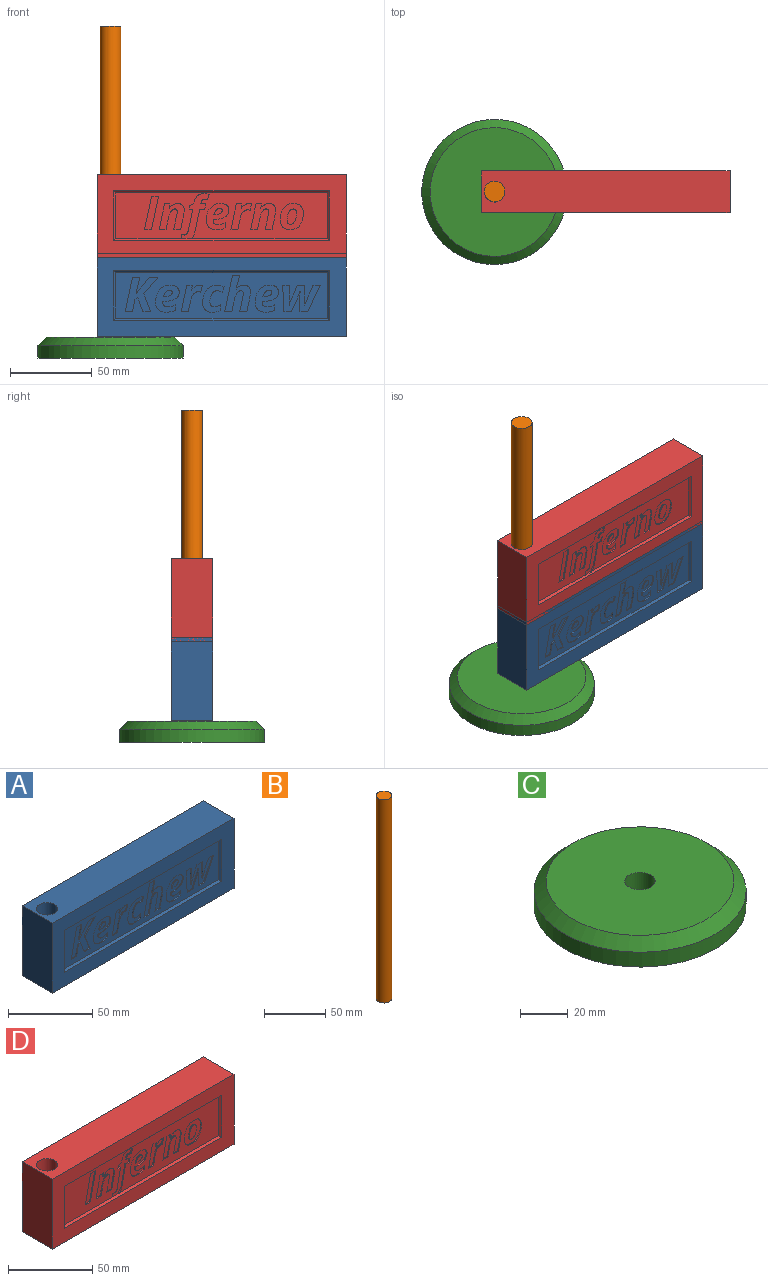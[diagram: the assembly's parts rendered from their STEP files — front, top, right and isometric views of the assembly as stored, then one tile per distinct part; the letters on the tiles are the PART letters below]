
ASSEMBLY  parts=4 mates=5
PART A: 157 faces, bbox 152.4x25.4x50.8 mm
  f0: plane 129.54x27.94mm, normal (0,-1,0), area 2509.1mm2, adj f8,f9,f10,f11,f12,f13,f14,f15
  f1: plane 152.4x50.8mm, normal (0,-1,0), area 3716.1mm2, adj f2,f3,f4,f5,f8,f9,f10,f11
  f2: plane 50.8x25.4mm, normal (1,0,0), area 1290.3mm2, adj f1,f3,f5,f6
  f3: plane 152.4x25.4mm, normal (0,0,1), area 3744.3mm2, adj f1,f2,f4,f6,f7
  f4: plane 50.8x25.4mm, normal (-1,0,0), area 1290.3mm2, adj f1,f3,f5,f6
  f5: plane 152.4x25.4mm, normal (0,0,-1), area 3744.3mm2, adj f1,f2,f4,f6,f7
  f6: plane 152.4x50.8mm, normal (0,1,0), area 7741.9mm2, adj f2,f3,f4,f5
  f7: cylinder r=6.35mm len=50.8mm, axis (0,0,1), area 2026.8mm2, adj f3,f5
  f8: plane 30.48x1.27mm, normal (0.71,-0.71,0), area 52.5mm2, adj f0,f1,f9,f10
  f9: plane 132.08x1.27mm, normal (0,-0.71,-0.71), area 234.9mm2, adj f0,f1,f8,f11
  f10: plane 132.08x1.27mm, normal (0,-0.71,0.71), area 234.9mm2, adj f0,f1,f8,f11
  f11: plane 30.48x1.27mm, normal (-0.71,-0.71,0), area 52.5mm2, adj f0,f1,f9,f10
  f12: plane 4.87x0.76mm, normal (0,0,1), area 3.7mm2, adj f0,f13,f24,f25
  f13: plane 10.97x4.19mm, normal (-0.93,0,-0.36), area 8.9mm2, adj f0,f12,f14,f25
  f14: plane 10.08x8.55mm, normal (-0.76,0,0.65), area 10.1mm2, adj f0,f13,f15,f25
  f15: plane 5.2x0.76mm, normal (0,0,-1), area 4mm2, adj f0,f14,f16,f25
  f16: plane 7.15x5.89mm, normal (0.77,0,-0.64), area 7.1mm2, adj f0,f15,f17,f25
  f17: plane 2.95x2.27mm, normal (0.79,0,-0.61), area 2.8mm2, adj f0,f16,f18,f25
  f18: plane 10.11x2.19mm, normal (-0.98,0,0.21), area 7.9mm2, adj f0,f17,f19,f25
  f19: plane 4.41x0.76mm, normal (0,0,-1), area 3.4mm2, adj f0,f18,f20,f25
  f20: plane 21.05x4.45mm, normal (0.98,0,-0.21), area 16.4mm2, adj f0,f19,f21,f25
  f21: plane 4.39x0.76mm, normal (0,0,1), area 3.3mm2, adj f0,f20,f22,f25
  f22: plane 7.51x1.57mm, normal (-0.98,0,0.2), area 5.8mm2, adj f0,f21,f23,f25
  f23: plane 1.8x1.01mm, normal (-0.49,0,0.87), area 1.6mm2, adj f0,f22,f24,f25
  f24: plane 8.52x3.04mm, normal (0.94,0,0.34), area 6.9mm2, adj f0,f12,f23,f25
  f25: plane 21.05x20.02mm, normal (0,-1,0), area 197.8mm2, adj f12,f13,f14,f15,f16,f17,f18,f19
  f26: extruded ~4.7x1.63mm, area 3.9mm2, adj f0,f27,f49,f50
  f27: extruded ~5.61x1.24mm, area 4.4mm2, adj f0,f26,f28,f50
  f28: plane 3.27x0.76mm, normal (-1,0,0), area 2.5mm2, adj f0,f27,f29,f50
  f29: extruded ~2.47x0.97mm, area 2mm2, adj f0,f28,f30,f50
  f30: extruded ~2.28x0.76mm, area 1.8mm2, adj f0,f29,f31,f50
  f31: extruded ~2.12x0.76mm, area 1.8mm2, adj f0,f30,f32,f50
  f32: extruded ~2.06x0.76mm, area 1.7mm2, adj f0,f31,f33,f50
  f33: plane 0.76x0.29mm, normal (-1,0,0), area 0.2mm2, adj f0,f32,f34,f50
  f34: plane 0.76x0.3mm, normal (-1,0,0.09), area 0.2mm2, adj f0,f33,f35,f50
  f35: plane 0.76x0.74mm, normal (0,0,1), area 0.6mm2, adj f0,f34,f36,f50
  f36: extruded ~6.87x1.46mm, area 5.4mm2, adj f0,f35,f37,f50
  f37: extruded ~4.15x2.4mm, area 3.8mm2, adj f0,f36,f38,f50
  f38: extruded ~3.22x1.42mm, area 2.8mm2, adj f0,f37,f39,f50
  f39: extruded ~3.98x1.17mm, area 3.2mm2, adj f0,f38,f40,f50
  f40: extruded ~4.59x1.29mm, area 3.7mm2, adj f0,f39,f41,f50
  f41: extruded ~3.74x3.22mm, area 3.8mm2, adj f0,f40,f42,f50
  f42: extruded ~5.43x1.19mm, area 4.3mm2, adj f0,f41,f49,f50
  f43: extruded ~2.39x1.15mm, area 2.1mm2, adj f44,f48,f50,f51
  f44: extruded ~1.51x1.37mm, area 1.8mm2, adj f43,f45,f50,f51
  f45: extruded ~1.89x1.24mm, area 1.8mm2, adj f44,f46,f50,f51
  f46: extruded ~3.48x0.76mm, area 2.7mm2, adj f45,f47,f50,f51
  f47: plane 0.76x0.65mm, normal (0,0,-1), area 0.5mm2, adj f46,f48,f50,f51
  f48: extruded ~2.81x1.47mm, area 2.4mm2, adj f43,f47,f50,f51
  f49: extruded ~4.59x1.67mm, area 3.8mm2, adj f0,f26,f42,f50
  f50: plane 16.68x14.39mm, normal (0,-1,0), area 145.3mm2, adj f26,f27,f28,f29,f30,f31,f32,f33
  f51: plane 5.37x3.96mm, normal (0,-1,0), area 14.5mm2, adj f43,f44,f45,f46,f47,f48
  f52: extruded ~4.7x1.63mm, area 3.9mm2, adj f0,f53,f75,f76
  f53: extruded ~5.61x1.24mm, area 4.4mm2, adj f0,f52,f54,f76
  f54: plane 3.27x0.76mm, normal (-1,0,0), area 2.5mm2, adj f0,f53,f55,f76
  f55: extruded ~2.47x0.97mm, area 2mm2, adj f0,f54,f56,f76
  f56: extruded ~2.28x0.76mm, area 1.8mm2, adj f0,f55,f57,f76
  f57: extruded ~2.12x0.76mm, area 1.8mm2, adj f0,f56,f58,f76
  f58: extruded ~2.06x0.76mm, area 1.7mm2, adj f0,f57,f59,f76
  f59: plane 0.76x0.29mm, normal (-1,0,0), area 0.2mm2, adj f0,f58,f60,f76
  f60: plane 0.76x0.3mm, normal (-1,0,0.09), area 0.2mm2, adj f0,f59,f61,f76
  f61: plane 0.76x0.74mm, normal (0,0,1), area 0.6mm2, adj f0,f60,f62,f76
  f62: extruded ~6.87x1.46mm, area 5.4mm2, adj f0,f61,f63,f76
  f63: extruded ~4.15x2.4mm, area 3.8mm2, adj f0,f62,f64,f76
  f64: extruded ~3.22x1.42mm, area 2.8mm2, adj f0,f63,f65,f76
  f65: extruded ~3.98x1.17mm, area 3.2mm2, adj f0,f64,f66,f76
  f66: extruded ~4.59x1.29mm, area 3.7mm2, adj f0,f65,f67,f76
  f67: extruded ~3.74x3.22mm, area 3.8mm2, adj f0,f66,f68,f76
  f68: extruded ~5.43x1.19mm, area 4.3mm2, adj f0,f67,f75,f76
  f69: extruded ~2.39x1.15mm, area 2.1mm2, adj f70,f74,f76,f77
  f70: extruded ~1.51x1.37mm, area 1.8mm2, adj f69,f71,f76,f77
  f71: extruded ~1.89x1.24mm, area 1.8mm2, adj f70,f72,f76,f77
  f72: extruded ~3.48x0.76mm, area 2.7mm2, adj f71,f73,f76,f77
  f73: plane 0.76x0.65mm, normal (0,0,-1), area 0.5mm2, adj f72,f74,f76,f77
  f74: extruded ~2.81x1.47mm, area 2.4mm2, adj f69,f73,f76,f77
  f75: extruded ~4.59x1.67mm, area 3.8mm2, adj f0,f52,f68,f76
  f76: plane 16.68x14.39mm, normal (0,-1,0), area 145.3mm2, adj f52,f53,f54,f55,f56,f57,f58,f59
  f77: plane 5.37x3.96mm, normal (0,-1,0), area 14.5mm2, adj f69,f70,f71,f72,f73,f74
  f78: extruded ~4.59x1.77mm, area 3.8mm2, adj f0,f79,f103,f104
  f79: plane 0.76x0.09mm, normal (0,0,1), area 0.1mm2, adj f0,f78,f80,f104
  f80: extruded ~4.9x0.76mm, area 3.7mm2, adj f0,f79,f81,f104
  f81: plane 7.49x0.76mm, normal (1,0,0.01), area 5.7mm2, adj f0,f80,f82,f104
  f82: plane 4.75x0.76mm, normal (0,0,1), area 3.6mm2, adj f0,f81,f83,f104
  f83: plane 16.09x7.63mm, normal (-0.9,0,0.43), area 13.6mm2, adj f0,f82,f84,f104
  f84: plane 4.42x0.76mm, normal (0,0,-1), area 3.4mm2, adj f0,f83,f85,f104
  f85: plane 7.13x3.15mm, normal (0.91,0,-0.4), area 5.9mm2, adj f0,f84,f86,f104
  f86: extruded ~3.71x1.37mm, area 3mm2, adj f0,f85,f87,f104
  f87: plane 1.15x0.76mm, normal (0.94,0,-0.33), area 0.9mm2, adj f0,f86,f88,f104
  f88: plane 0.76x0.09mm, normal (0,0,-1), area 0.1mm2, adj f0,f87,f89,f104
  f89: extruded ~4.27x0.76mm, area 3.3mm2, adj f0,f88,f90,f104
  f90: plane 7.72x0.76mm, normal (-1,0,0), area 5.9mm2, adj f0,f89,f91,f104
  f91: plane 4.72x0.76mm, normal (0,0,-1), area 3.6mm2, adj f0,f90,f92,f104
  f92: plane 7.72x3.33mm, normal (0.92,0,-0.4), area 6.4mm2, adj f0,f91,f93,f104
  f93: extruded ~1.71x0.76mm, area 1.4mm2, adj f0,f92,f94,f104
  f94: extruded ~1.96x0.76mm, area 1.6mm2, adj f0,f93,f95,f104
  f95: extruded ~0.76x0.6mm, area 0.5mm2, adj f0,f94,f96,f104
  f96: plane 0.76x0.06mm, normal (0,0,-1), area 0mm2, adj f0,f95,f97,f104
  f97: plane 2.46x0.76mm, normal (-1,0,0.04), area 1.9mm2, adj f0,f96,f98,f104
  f98: plane 2.4x0.76mm, normal (-1,0,0.02), area 1.8mm2, adj f0,f97,f99,f104
  f99: plane 7.13x0.76mm, normal (-1,0,-0.01), area 5.4mm2, adj f0,f98,f100,f104
  f100: plane 4.04x0.76mm, normal (0,0,-1), area 3.1mm2, adj f0,f99,f101,f104
  f101: plane 16.09x0.76mm, normal (1,0,0.05), area 12.3mm2, adj f0,f100,f102,f104
  f102: plane 4.67x0.76mm, normal (0,0,1), area 3.6mm2, adj f0,f101,f103,f104
  f103: plane 7.79x3.35mm, normal (-0.92,0,0.4), area 6.5mm2, adj f0,f78,f102,f104
  f104: plane 22.93x16.09mm, normal (0,-1,0), area 215.7mm2, adj f78,f79,f80,f81,f82,f83,f84,f85
  f105: plane 4.33x0.76mm, normal (0,0,1), area 3.3mm2, adj f0,f106,f123,f124
  f106: plane 9.17x1.92mm, normal (-0.98,0,0.2), area 7.1mm2, adj f0,f105,f107,f124
  f107: extruded ~2.59x0.76mm, area 2mm2, adj f0,f106,f108,f124
  f108: extruded ~3.43x1.09mm, area 2.8mm2, adj f0,f107,f109,f124
  f109: extruded ~3.07x1.2mm, area 2.6mm2, adj f0,f108,f110,f124
  f110: extruded ~2.54x0.76mm, area 2mm2, adj f0,f109,f111,f124
  f111: extruded ~1.99x1.78mm, area 2mm2, adj f0,f110,f112,f124
  f112: plane 0.76x0.12mm, normal (0,0,-1), area 0.1mm2, adj f0,f111,f113,f124
  f113: extruded ~4.45x1.24mm, area 3.5mm2, adj f0,f112,f114,f124
  f114: extruded ~4x0.87mm, area 3.1mm2, adj f0,f113,f115,f124
  f115: plane 4.33x0.76mm, normal (0,0,-1), area 3.3mm2, adj f0,f114,f116,f124
  f116: plane 22.4x4.75mm, normal (0.98,0,-0.21), area 17.4mm2, adj f0,f115,f117,f124
  f117: plane 4.33x0.76mm, normal (0,0,1), area 3.3mm2, adj f0,f116,f118,f124
  f118: plane 6.67x1.41mm, normal (-0.98,0,0.21), area 5.2mm2, adj f0,f117,f119,f124
  f119: extruded ~4.58x1.7mm, area 3.7mm2, adj f0,f118,f120,f124
  f120: extruded ~2.4x1.64mm, area 2.3mm2, adj f0,f119,f121,f124
  f121: extruded ~1.77x1.56mm, area 2.1mm2, adj f0,f120,f122,f124
  f122: extruded ~1.71x0.76mm, area 1.3mm2, adj f0,f121,f123,f124
  f123: plane 9.4x1.97mm, normal (0.98,0,-0.21), area 7.3mm2, adj f0,f105,f122,f124
  f124: plane 22.4x15.78mm, normal (0,-1,0), area 179.3mm2, adj f105,f106,f107,f108,f109,f110,f111,f112
  f125: extruded ~4.44x1.55mm, area 3.7mm2, adj f0,f126,f142,f143
  f126: extruded ~4.84x1.14mm, area 3.8mm2, adj f0,f125,f127,f143
  f127: plane 3.54x0.76mm, normal (-1,0,0), area 2.7mm2, adj f0,f126,f128,f143
  f128: extruded ~1.93x0.84mm, area 1.6mm2, adj f0,f127,f129,f143
  f129: extruded ~2.03x0.76mm, area 1.6mm2, adj f0,f128,f130,f143
  f130: extruded ~1.82x0.76mm, area 1.5mm2, adj f0,f129,f131,f143
  f131: extruded ~2.08x0.76mm, area 1.7mm2, adj f0,f130,f132,f143
  f132: extruded ~3.45x0.76mm, area 2.7mm2, adj f0,f131,f133,f143
  f133: extruded ~2.53x1.54mm, area 2.3mm2, adj f0,f132,f134,f143
  f134: extruded ~2.21x0.92mm, area 1.9mm2, adj f0,f133,f135,f143
  f135: extruded ~1.7x0.76mm, area 1.3mm2, adj f0,f134,f136,f143
  f136: extruded ~1.53x0.76mm, area 1.2mm2, adj f0,f135,f137,f143
  f137: plane 3.29x1.32mm, normal (-0.93,0,0.37), area 2.7mm2, adj f0,f136,f138,f143
  f138: extruded ~4.72x1.04mm, area 3.7mm2, adj f0,f137,f139,f143
  f139: extruded ~4.43x1.36mm, area 3.6mm2, adj f0,f138,f140,f143
  f140: extruded ~3.86x3.02mm, area 3.8mm2, adj f0,f139,f141,f143
  f141: extruded ~5.55x1.07mm, area 4.3mm2, adj f0,f140,f142,f143
  f142: extruded ~4.37x1.55mm, area 3.6mm2, adj f0,f125,f141,f143
  f143: plane 16.68x13.24mm, normal (0,-1,0), area 108mm2, adj f125,f126,f127,f128,f129,f130,f131,f132
  f144: extruded ~1.38x0.76mm, area 1.1mm2, adj f0,f145,f155,f156
  f145: extruded ~5.08x3.28mm, area 4.8mm2, adj f0,f144,f146,f156
  f146: plane 0.76x0.09mm, normal (0,0,-1), area 0.1mm2, adj f0,f145,f147,f156
  f147: plane 2.98x0.76mm, normal (-0.99,0,0.1), area 2.3mm2, adj f0,f146,f148,f156
  f148: plane 3.31x0.76mm, normal (0,0,-1), area 2.5mm2, adj f0,f147,f149,f156
  f149: plane 16.09x3.41mm, normal (0.98,0,-0.21), area 12.5mm2, adj f0,f148,f150,f156
  f150: plane 4.33x0.76mm, normal (0,0,1), area 3.3mm2, adj f0,f149,f151,f156
  f151: plane 7.2x1.53mm, normal (-0.98,0,0.21), area 5.6mm2, adj f0,f150,f152,f156
  f152: extruded ~3.78x1.79mm, area 3.2mm2, adj f0,f151,f153,f156
  f153: extruded ~2.93x1.32mm, area 2.5mm2, adj f0,f152,f154,f156
  f154: extruded ~1.44x0.76mm, area 1.1mm2, adj f0,f153,f155,f156
  f155: plane 4.17x0.95mm, normal (-0.98,0,0.22), area 3.3mm2, adj f0,f144,f154,f156
  f156: plane 16.39x12.97mm, normal (0,-1,0), area 89.8mm2, adj f144,f145,f146,f147,f148,f149,f150,f151
PART B: 3 faces, bbox 12.7x12.7x203.2 mm
  f0: cylinder r=6.35mm len=203.2mm, axis (0,0,-1), area 8107.3mm2, adj f1,f2
  f1: plane 12.7x12.7mm, normal (0,0,1), area 126.7mm2, adj f0
  f2: plane 12.7x12.7mm, normal (0,0,-1), area 126.7mm2, adj f0
PART C: 6 faces, bbox 88.9x88.9x12.7 mm
  f0: cylinder r=44.45mm len=88.9mm, axis (0,0,-1), area 2128.2mm2, adj f2,f3
  f1: plane 78.74x78.74mm, normal (0,0,1), area 4742.8mm2, adj f3,f4
  f2: plane 88.9x88.9mm, normal (0,0,-1), area 6207.2mm2, adj f0
  f3: cone r=39.37mm half-angle=45deg, axis (0,0,-1), area 1891.8mm2, adj f0,f1
  f4: cylinder r=6.35mm len=12.7mm, axis (0,0,1), area 505.7mm2, adj f1,f5
  f5: plane 12.7x12.7mm, normal (0,0,1), area 126.7mm2, adj f4
PART D: 137 faces, bbox 152.4x25.4x50.8 mm
  f0: plane 129.54x28.09mm, normal (0,-1,0), area 2679.9mm2, adj f8,f9,f10,f11,f12,f13,f14,f15
  f1: plane 152.4x50.8mm, normal (0,-1,0), area 3716.1mm2, adj f2,f3,f4,f5,f8,f9,f10,f11
  f2: plane 50.8x25.4mm, normal (1,0,0), area 1290.3mm2, adj f1,f3,f5,f6
  f3: plane 152.4x25.4mm, normal (0,0,1), area 3744.3mm2, adj f1,f2,f4,f6,f7
  f4: plane 50.8x25.4mm, normal (-1,0,0), area 1290.3mm2, adj f1,f3,f5,f6
  f5: plane 152.4x25.4mm, normal (0,0,-1), area 3744.3mm2, adj f1,f2,f4,f6,f7
  f6: plane 152.4x50.8mm, normal (0,1,0), area 7741.9mm2, adj f2,f3,f4,f5
  f7: cylinder r=6.35mm len=50.8mm, axis (0,0,1), area 2026.8mm2, adj f3,f5
  f8: plane 30.48x1.27mm, normal (0.71,-0.71,0), area 52.5mm2, adj f0,f1,f9,f10
  f9: plane 132.08x1.27mm, normal (0,-0.71,-0.71), area 234.9mm2, adj f0,f1,f8,f11
  f10: plane 132.08x1.27mm, normal (0,-0.71,0.71), area 234.9mm2, adj f0,f1,f8,f11,f131
  f11: plane 30.48x1.27mm, normal (-0.71,-0.71,0), area 52.5mm2, adj f0,f1,f9,f10
  f12: extruded ~4.56x1.58mm, area 3.8mm2, adj f0,f13,f35,f36
  f13: extruded ~5.45x1.2mm, area 4.3mm2, adj f0,f12,f14,f36
  f14: plane 3.18x0.76mm, normal (-1,0,0), area 2.4mm2, adj f0,f13,f15,f36
  f15: extruded ~2.4x0.94mm, area 2mm2, adj f0,f14,f16,f36
  f16: extruded ~2.21x0.76mm, area 1.7mm2, adj f0,f15,f17,f36
  f17: extruded ~2.06x0.76mm, area 1.7mm2, adj f0,f16,f18,f36
  f18: extruded ~2x0.76mm, area 1.7mm2, adj f0,f17,f19,f36
  f19: plane 0.76x0.28mm, normal (-1,0,0), area 0.2mm2, adj f0,f18,f20,f36
  f20: plane 0.76x0.3mm, normal (-1,0,0.09), area 0.2mm2, adj f0,f19,f21,f36
  f21: plane 0.76x0.72mm, normal (0,0,1), area 0.5mm2, adj f0,f20,f22,f36
  f22: extruded ~6.67x1.42mm, area 5.3mm2, adj f0,f21,f23,f36
  f23: extruded ~4.03x2.33mm, area 3.7mm2, adj f0,f22,f24,f36
  f24: extruded ~3.13x1.38mm, area 2.7mm2, adj f0,f23,f25,f36
  f25: extruded ~3.86x1.14mm, area 3.1mm2, adj f0,f24,f26,f36
  f26: extruded ~4.46x1.25mm, area 3.6mm2, adj f0,f25,f27,f36
  f27: extruded ~3.64x3.13mm, area 3.7mm2, adj f0,f26,f28,f36
  f28: extruded ~5.28x1.15mm, area 4.2mm2, adj f0,f27,f35,f36
  f29: extruded ~2.32x1.12mm, area 2mm2, adj f30,f34,f36,f37
  f30: extruded ~1.47x1.33mm, area 1.7mm2, adj f29,f31,f36,f37
  f31: extruded ~1.84x1.21mm, area 1.8mm2, adj f30,f32,f36,f37
  f32: extruded ~3.38x0.76mm, area 2.7mm2, adj f31,f33,f36,f37
  f33: plane 0.76x0.63mm, normal (0,0,-1), area 0.5mm2, adj f32,f34,f36,f37
  f34: extruded ~2.73x1.43mm, area 2.4mm2, adj f29,f33,f36,f37
  f35: extruded ~4.46x1.62mm, area 3.7mm2, adj f0,f12,f28,f36
  f36: plane 16.21x13.98mm, normal (0,-1,0), area 137.1mm2, adj f12,f13,f14,f15,f16,f17,f18,f19
  f37: plane 5.21x3.84mm, normal (0,-1,0), area 13.7mm2, adj f29,f30,f31,f32,f33,f34
  f38: plane 4.21x0.76mm, normal (0,0,1), area 3.2mm2, adj f0,f39,f54,f55
  f39: plane 8.91x1.86mm, normal (-0.98,0,0.2), area 6.9mm2, adj f0,f38,f40,f55
  f40: extruded ~2.51x0.76mm, area 1.9mm2, adj f0,f39,f41,f55
  f41: extruded ~3.34x1.06mm, area 2.7mm2, adj f0,f40,f42,f55
  f42: extruded ~2.98x1.17mm, area 2.5mm2, adj f0,f41,f43,f55
  f43: extruded ~4.97x3.19mm, area 4.7mm2, adj f0,f42,f44,f55
  f44: plane 0.76x0.09mm, normal (0,0,-1), area 0.1mm2, adj f0,f43,f45,f55
  f45: plane 2.9x0.76mm, normal (-0.99,0,0.1), area 2.2mm2, adj f0,f44,f46,f55
  f46: plane 3.22x0.76mm, normal (0,0,-1), area 2.5mm2, adj f0,f45,f47,f55
  f47: plane 15.63x3.31mm, normal (0.98,0,-0.21), area 12.2mm2, adj f0,f46,f48,f55
  f48: plane 4.21x0.76mm, normal (0,0,1), area 3.2mm2, adj f0,f47,f49,f55
  f49: plane 6.48x1.37mm, normal (-0.98,0,0.21), area 5mm2, adj f0,f48,f50,f55
  f50: extruded ~4.45x1.65mm, area 3.6mm2, adj f0,f49,f51,f55
  f51: extruded ~2.33x1.6mm, area 2.2mm2, adj f0,f50,f52,f55
  f52: extruded ~1.72x1.51mm, area 2mm2, adj f0,f51,f53,f55
  f53: extruded ~1.66x0.76mm, area 1.3mm2, adj f0,f52,f54,f55
  f54: plane 9.13x1.92mm, normal (0.98,0,-0.21), area 7.1mm2, adj f0,f38,f53,f55
  f55: plane 15.93x15.33mm, normal (0,-1,0), area 142mm2, adj f38,f39,f40,f41,f42,f43,f44,f45
  f56: extruded ~1.34x0.76mm, area 1mm2, adj f0,f57,f67,f68
  f57: extruded ~4.94x3.19mm, area 4.7mm2, adj f0,f56,f58,f68
  f58: plane 0.76x0.09mm, normal (0,0,-1), area 0.1mm2, adj f0,f57,f59,f68
  f59: plane 2.9x0.76mm, normal (-0.99,0,0.1), area 2.2mm2, adj f0,f58,f60,f68
  f60: plane 3.22x0.76mm, normal (0,0,-1), area 2.5mm2, adj f0,f59,f61,f68
  f61: plane 15.63x3.31mm, normal (0.98,0,-0.21), area 12.2mm2, adj f0,f60,f62,f68
  f62: plane 4.21x0.76mm, normal (0,0,1), area 3.2mm2, adj f0,f61,f63,f68
  f63: plane 6.99x1.49mm, normal (-0.98,0,0.21), area 5.4mm2, adj f0,f62,f64,f68
  f64: extruded ~3.67x1.74mm, area 3.1mm2, adj f0,f63,f65,f68
  f65: extruded ~2.85x1.28mm, area 2.4mm2, adj f0,f64,f66,f68
  f66: extruded ~1.4x0.76mm, area 1.1mm2, adj f0,f65,f67,f68
  f67: plane 4.05x0.92mm, normal (-0.98,0,0.22), area 3.2mm2, adj f0,f56,f66,f68
  f68: plane 15.93x12.6mm, normal (0,-1,0), area 84.8mm2, adj f56,f57,f58,f59,f60,f61,f62,f63
  f69: plane 4.21x0.76mm, normal (0,0,1), area 3.2mm2, adj f0,f70,f85,f86
  f70: plane 8.91x1.86mm, normal (-0.98,0,0.2), area 6.9mm2, adj f0,f69,f71,f86
  f71: extruded ~2.51x0.76mm, area 1.9mm2, adj f0,f70,f72,f86
  f72: extruded ~3.34x1.06mm, area 2.7mm2, adj f0,f71,f73,f86
  f73: extruded ~2.98x1.17mm, area 2.5mm2, adj f0,f72,f74,f86
  f74: extruded ~4.97x3.19mm, area 4.7mm2, adj f0,f73,f75,f86
  f75: plane 0.76x0.09mm, normal (0,0,-1), area 0.1mm2, adj f0,f74,f76,f86
  f76: plane 2.9x0.76mm, normal (-0.99,0,0.1), area 2.2mm2, adj f0,f75,f77,f86
  f77: plane 3.22x0.76mm, normal (0,0,-1), area 2.5mm2, adj f0,f76,f78,f86
  f78: plane 15.63x3.31mm, normal (0.98,0,-0.21), area 12.2mm2, adj f0,f77,f79,f86
  f79: plane 4.21x0.76mm, normal (0,0,1), area 3.2mm2, adj f0,f78,f80,f86
  f80: plane 6.48x1.37mm, normal (-0.98,0,0.21), area 5mm2, adj f0,f79,f81,f86
  f81: extruded ~4.45x1.65mm, area 3.6mm2, adj f0,f80,f82,f86
  f82: extruded ~2.33x1.6mm, area 2.2mm2, adj f0,f81,f83,f86
  f83: extruded ~1.72x1.51mm, area 2mm2, adj f0,f82,f84,f86
  f84: extruded ~1.66x0.76mm, area 1.3mm2, adj f0,f83,f85,f86
  f85: plane 9.13x1.92mm, normal (0.98,0,-0.21), area 7.1mm2, adj f0,f69,f84,f86
  f86: plane 15.93x15.33mm, normal (0,-1,0), area 142mm2, adj f69,f70,f71,f72,f73,f74,f75,f76
  f87: extruded ~5.23x0.99mm, area 4.1mm2, adj f0,f88,f104,f105
  f88: extruded ~4.54x1.6mm, area 3.8mm2, adj f0,f87,f89,f105
  f89: extruded ~4.33x1.65mm, area 3.6mm2, adj f0,f88,f90,f105
  f90: extruded ~4.42x1.28mm, area 3.6mm2, adj f0,f89,f91,f105
  f91: extruded ~3.61x2.89mm, area 3.6mm2, adj f0,f90,f92,f105
  f92: extruded ~5.31x1mm, area 4.1mm2, adj f0,f91,f93,f105
  f93: extruded ~4.37x1.63mm, area 3.7mm2, adj f0,f92,f94,f105
  f94: extruded ~4.36x1.64mm, area 3.6mm2, adj f0,f93,f95,f105
  f95: extruded ~4.42x1.25mm, area 3.6mm2, adj f0,f94,f104,f105
  f96: extruded ~2.76x2mm, area 3mm2, adj f97,f103,f105,f106
  f97: extruded ~3.33x0.76mm, area 2.6mm2, adj f96,f98,f105,f106
  f98: extruded ~2.39x1.31mm, area 2.1mm2, adj f97,f99,f105,f106
  f99: extruded ~1.89x0.86mm, area 1.6mm2, adj f98,f100,f105,f106
  f100: extruded ~2.59x2.1mm, area 2.9mm2, adj f99,f101,f105,f106
  f101: extruded ~3.4x0.76mm, area 2.6mm2, adj f100,f102,f105,f106
  f102: extruded ~2.5x1.36mm, area 2.2mm2, adj f101,f103,f105,f106
  f103: extruded ~1.88x0.85mm, area 1.6mm2, adj f96,f102,f105,f106
  f104: extruded ~3.53x2.85mm, area 3.5mm2, adj f0,f87,f95,f105
  f105: plane 16.21x14.24mm, normal (0,-1,0), area 143.7mm2, adj f87,f88,f89,f90,f91,f92,f93,f94
  f106: plane 9.34x5.76mm, normal (0,-1,0), area 41.7mm2, adj f96,f97,f98,f99,f100,f101,f102,f103
  f107: plane 3.38x0.76mm, normal (1,0,0), area 2.6mm2, adj f0,f108,f129,f130,f131
  f108: extruded ~2.43x0.76mm, area 1.9mm2, adj f107,f109,f130,f131
  f109: extruded ~5.64x5.19mm, area 6.4mm2, adj f0,f108,f110,f130,f131
  f110: plane 14.12x3.01mm, normal (-0.98,0,0.21), area 11mm2, adj f0,f109,f111,f130
  f111: plane 3.07x0.76mm, normal (0,0,1), area 2.3mm2, adj f0,f110,f112,f130
  f112: plane 3.2x0.76mm, normal (-0.98,0,0.21), area 2.5mm2, adj f0,f111,f113,f130
  f113: plane 3.06x0.76mm, normal (0,0,-1), area 2.3mm2, adj f0,f112,f114,f130
  f114: plane 0.87x0.76mm, normal (-0.98,0,0.19), area 0.7mm2, adj f0,f113,f115,f130
  f115: extruded ~1.47x0.76mm, area 1.2mm2, adj f0,f114,f116,f130
  f116: extruded ~1.29x0.76mm, area 1.1mm2, adj f0,f115,f117,f130
  f117: extruded ~1.86x0.76mm, area 1.5mm2, adj f0,f116,f118,f130
  f118: plane 3.13x1.12mm, normal (-0.94,0,0.34), area 2.5mm2, adj f0,f117,f119,f130
  f119: extruded ~3.28x0.76mm, area 2.6mm2, adj f0,f118,f120,f130
  f120: extruded ~3.82x1.22mm, area 3.1mm2, adj f0,f119,f121,f130
  f121: extruded ~3.88x1.94mm, area 3.4mm2, adj f0,f120,f122,f130
  f122: plane 1.17x0.76mm, normal (0.98,0,-0.21), area 0.9mm2, adj f0,f121,f123,f130
  f123: plane 2.56x1.18mm, normal (0.42,0,-0.91), area 2.1mm2, adj f0,f122,f124,f130
  f124: plane 2.03x0.76mm, normal (0.98,0,-0.2), area 1.6mm2, adj f0,f123,f125,f130
  f125: plane 2.28x0.76mm, normal (0,0,1), area 1.7mm2, adj f0,f124,f126,f130
  f126: plane 13.5x2.85mm, normal (0.98,0,-0.21), area 10.5mm2, adj f0,f125,f127,f130
  f127: extruded ~1.82x0.91mm, area 1.6mm2, adj f0,f126,f128,f130
  f128: extruded ~1.5x0.76mm, area 1.2mm2, adj f0,f127,f129,f130
  f129: extruded ~1.61x0.76mm, area 1.3mm2, adj f0,f107,f128,f130
  f130: plane 28.79x16.86mm, normal (0,-1,0), area 153.3mm2, adj f107,f108,f109,f110,f111,f112,f113,f114
  f131: plane 6.2x1.38mm, normal (0,1,0), area 5.9mm2, adj f10,f107,f108,f109
  f132: plane 20.45x4.36mm, normal (0.98,0,-0.21), area 15.9mm2, adj f0,f133,f135,f136
  f133: plane 4.26x0.76mm, normal (0,0,1), area 3.2mm2, adj f0,f132,f134,f136
  f134: plane 20.45x4.36mm, normal (-0.98,0,0.21), area 15.9mm2, adj f0,f133,f135,f136
  f135: plane 4.26x0.76mm, normal (0,0,-1), area 3.2mm2, adj f0,f132,f134,f136
  f136: plane 20.45x8.63mm, normal (0,-1,0), area 87.2mm2, adj f132,f133,f134,f135
PLACE A rot(axis=(1,0,0),0deg) t=(67.98,0,25.66)mm
PLACE B rot(axis=(1,0,0),180deg) t=(0,0,88.93)mm
PLACE C rot(axis=(1,0,0),0deg) t=(0,0,-12.7)mm
PLACE D rot(axis=(1,0,0),0deg) t=(67.98,0,74.35)mm
MATE slider B.f0 <-> D.f7  axis (0,0,1) through (0,0,190.53)mm
MATE cylindrical D.f7 <-> B.f0  axis (0,0,1) through (0,0,99.75)mm
MATE slider B.f0 <-> A.f7  axis (0,0,1) through (0,0,88.93)mm
MATE fastened B.f0 <-> C.f4  axis (0,0,-1) through (0,0,-12.67)mm
MATE cylindrical A.f7 <-> B.f0  axis (0,0,1) through (0,0,51.06)mm
